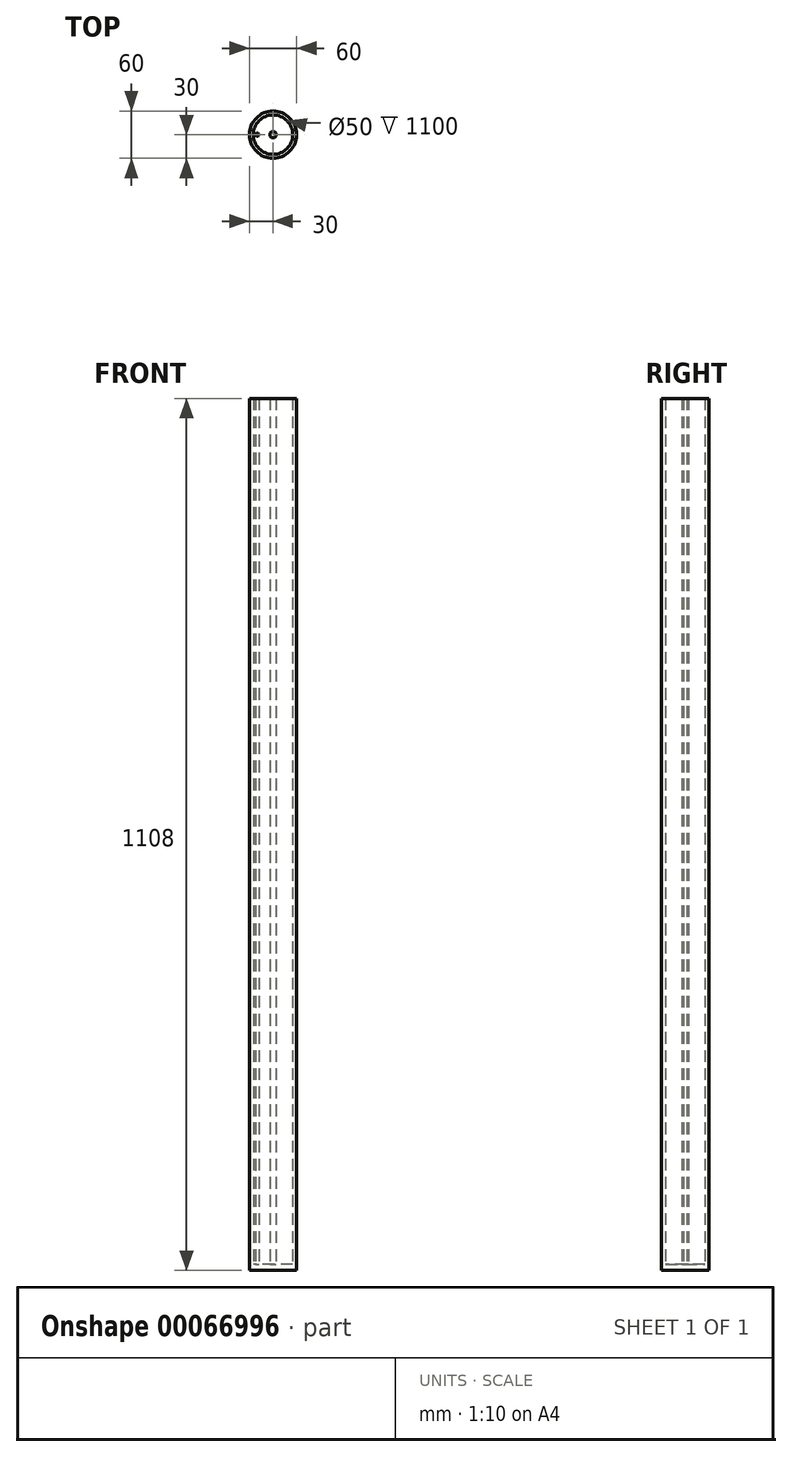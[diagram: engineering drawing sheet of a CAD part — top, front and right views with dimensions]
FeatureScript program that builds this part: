
annotation { "Feature Type Name" : "Feature", "Feature Type Description" : "" }
export const myFeature = defineFeature(function(context is Context, id is Id, definition is map)
    precondition{}
    {
        {
            var Q0;
            Q0=qCreatedBy(makeId("Top.planeOp"),FACE);
            var sketch = newSketch(context, id + "F0", { "sketchPlane" : qUnion([Q0])});
            skCircle(sketch, "E0", {"center": v(0, 0) * mm, "radius": 30 * mm});
            skCircle(sketch, "E1", {"center": v(0, 0) * mm, "radius": 25 * mm});
            skSolve(sketch);
        }
        {
            var Q0;
            Q0 = qSketchRegion(id + "F0", true);
            extrude(context, id + "F1", {"entities" : qUnion([Q0]), "depth" : 1100 * mm});
        }
        {
            var Q0;
            Q0=makeQuery(id+"F1.opExtrude","CAP_FACE",FACE,{"disambiguationData":[OSD([sQuery(id+"F0.wireOp",EDGE,"E0"),sQuery(id+"F0.wireOp",EDGE,"E1")])],"isStart":true});
            var sketch = newSketch(context, id + "F2", { "sketchPlane" : qUnion([Q0])});
            skCircle(sketch, "E2", {"center": v(0, 0) * mm, "radius": 30 * mm});
            skSolve(sketch);
        }
        {
            var Q0;
            Q0 = qSketchRegion(id + "F2", true);
            extrude(context, id + "F3", {"entities" : qUnion([Q0]), "operationType" : NewBodyOperationType.ADD, "depth" : 8 * mm});
        }
        {
            var Q0;
            Q0=makeQuery(id+"F3.opExtrude","CAP_FACE",FACE,{"disambiguationData":[OSD([sQuery(id+"F2.wireOp",EDGE,"E2")])],"isStart":false});
            var sketch = newSketch(context, id + "F4", { "sketchPlane" : qUnion([Q0])});
            skCircle(sketch, "E3", {"center": v(0, 0) * mm, "radius": 4 * mm});
            skCircle(sketch, "E4", {"center": v(-20, 0) * mm, "radius": 2 * mm});
            skSolve(sketch);
        }
        {
            var Q0;
            Q0 = qSketchRegion(id + "F4", true);
            extrude(context, id + "F5", {"entities" : qUnion([Q0]), "operationType" : NewBodyOperationType.ADD, "oppositeDirection" : true, "depth" : 1108 * mm});
        }
    });
